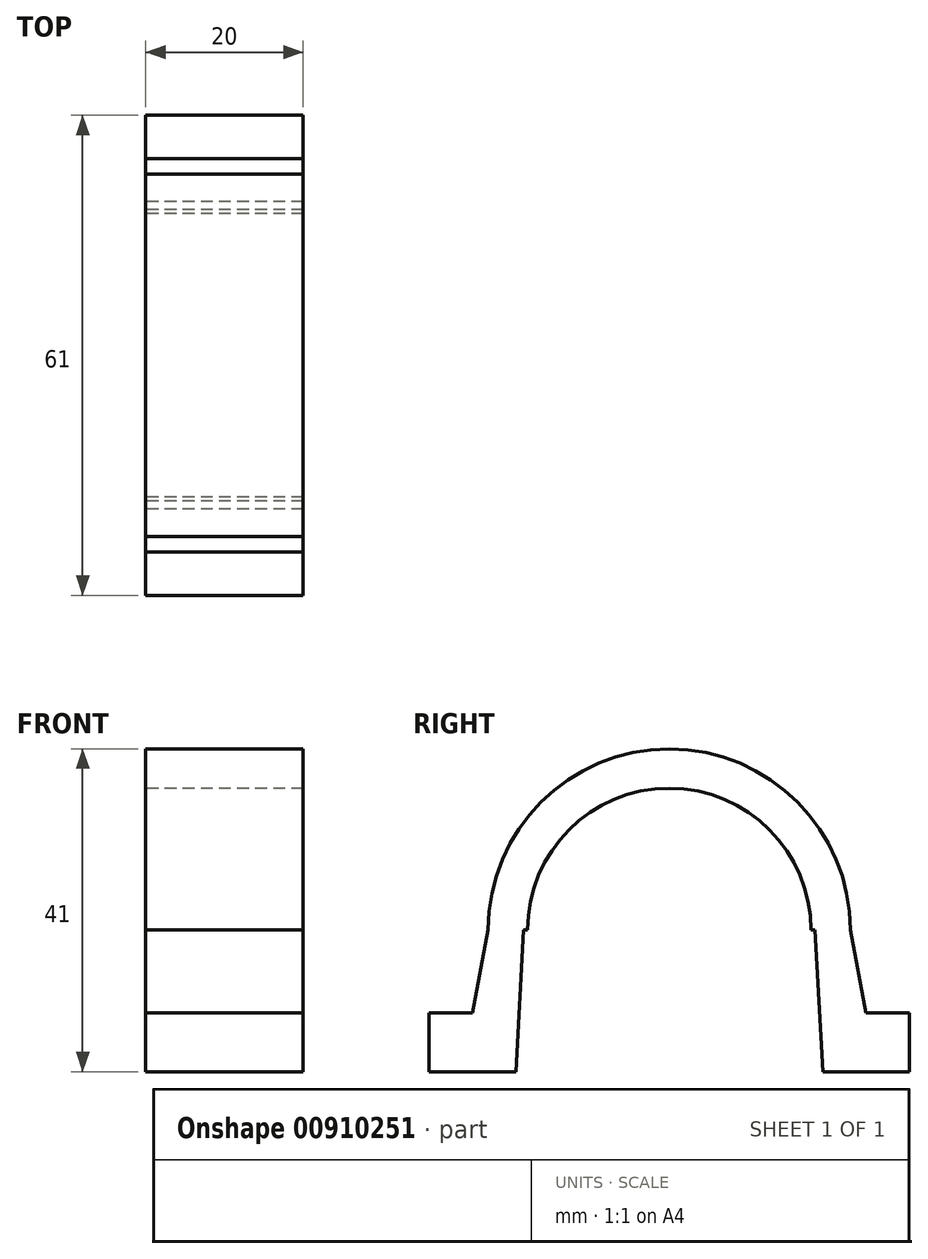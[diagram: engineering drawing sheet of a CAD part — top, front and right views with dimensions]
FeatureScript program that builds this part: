
annotation { "Feature Type Name" : "Feature", "Feature Type Description" : "" }
export const myFeature = defineFeature(function(context is Context, id is Id, definition is map)
    precondition{}
    {
        {
            var Q0;
            Q0=qCreatedBy(makeId("Right.planeOp"),FACE);
            var sketch = newSketch(context, id + "F0", { "sketchPlane" : qUnion([Q0])});
            skCircle(sketch, "E0", {"center": v(0, 0) * mm, "radius": 18 * mm});
            skCircle(sketch, "E1", {"center": v(0, 0) * mm, "radius": 23 * mm});
            skLineSegment(sketch, "E2.bottom", {"start": v(-30.5, -10) * mm, "end": v(30.5, -10) * mm});
            skLineSegment(sketch, "E2.top", {"start": v(-30.5, 10) * mm, "end": v(30.5, 10) * mm});
            skLineSegment(sketch, "E2.left", {"start": v(-30.5, -10) * mm, "end": v(-30.5, 10) * mm});
            skLineSegment(sketch, "E2.right", {"start": v(30.5, -10) * mm, "end": v(30.5, 10) * mm});
            skLineSegment(sketch, "E3", {"start": v(-30.5, 0) * mm, "end": v(30.5, 0) * mm});
            skLineSegment(sketch, "E4", {"start": v(0, 0) * mm, "end": v(0, -18) * mm});
            skPoint(sketch, "E4.endSnap0", {"position": v(0, -10) * mm});
            skLineSegment(sketch, "E5", {"start": v(0, -18) * mm, "end": v(30.5, -18) * mm});
            skLineSegment(sketch, "E6", {"start": v(0, -18) * mm, "end": v(-30.5, -18) * mm});
            skLineSegment(sketch, "E7", {"start": v(18, 0) * mm, "end": v(18.5, 0) * mm});
            skLineSegment(sketch, "E8", {"start": v(18.5, 0) * mm, "end": v(18.5, -18) * mm});
            skLineSegment(sketch, "E9", {"start": v(18.5, -18) * mm, "end": v(19.5, -18) * mm});
            skLineSegment(sketch, "E10", {"start": v(18.5, 0) * mm, "end": v(19.5, -18) * mm});
            skLineSegment(sketch, "E11", {"start": v(30.5, 0) * mm, "end": v(30.5, -18) * mm});
            skLineSegment(sketch, "E12", {"start": v(30.5, -18) * mm, "end": v(30.5, -10.5) * mm});
            skLineSegment(sketch, "E13", {"start": v(30.5, -10.5) * mm, "end": v(18.5, -10.5) * mm});
            skLineSegment(sketch, "E14", {"start": v(23, 0) * mm, "end": v(23, -10.5) * mm});
            skLineSegment(sketch, "E15", {"start": v(23, -10.5) * mm, "end": v(25, -10.5) * mm});
            skLineSegment(sketch, "E16", {"start": v(23, 0) * mm, "end": v(25, -10.5) * mm});
            skPoint(sketch, "E17.end.orphan", {"position": v(25, -18) * mm});
            skLineSegment(sketch, "E18.MirrorCS", {"start": v(-23, 0) * mm, "end": v(-25, -10.5) * mm});
            skLineSegment(sketch, "E19.MirrorCS", {"start": v(-30.5, -10.5) * mm, "end": v(-18.5, -10.5) * mm});
            skLineSegment(sketch, "E20.MirrorCS", {"start": v(-30.5, 0) * mm, "end": v(-30.5, -18) * mm});
            skLineSegment(sketch, "E21.MirrorCS", {"start": v(-18.5, 0) * mm, "end": v(-19.5, -18) * mm});
            skLineSegment(sketch, "E22.MirrorCS", {"start": v(-18, 0) * mm, "end": v(-18.5, 0) * mm});
            skSolve(sketch);
        }
        {
            var Q0;
            {var subQ4=sQuery(id+"F0.wireOp",EDGE,"E2.top");var subQ5=sQuery(id+"F0.wireOp",EDGE,"E0");var subQ6=makeQuery(id+"F0.imprint","INTERSECT",VERTEX,{"disambiguationData":[OD(0.0)],"derivedFrom":[subQ5,subQ4]});Q0=makeQuery(id+"F0.imprint","IMPRINT",FACE,{"disambiguationData":[TD([[makeQuery(id+"F0.imprint","IMPRINT",EDGE,{"disambiguationData":[TD([[subQ6,-1.0]])],"derivedFrom":subQ5}),-1.0]])]});}
            var Q1;
            {var subQ0=sQuery(id+"F0.wireOp",EDGE,"E2.top");var subQ1=sQuery(id+"F0.wireOp",EDGE,"E0");var subQ2=makeQuery(id+"F0.imprint","INTERSECT",VERTEX,{"disambiguationData":[OD(0.0)],"derivedFrom":[subQ1,subQ0]});Q1=makeQuery(id+"F0.imprint","IMPRINT",FACE,{"disambiguationData":[TD([[makeQuery(id+"F0.imprint","IMPRINT",EDGE,{"disambiguationData":[TD([[subQ2,1.0]])],"derivedFrom":subQ1}),-1.0]])]});}
            var Q2;
            {var subQ0=sQuery(id+"F0.wireOp",EDGE,"E3");var subQ6=sQuery(id+"F0.wireOp",EDGE,"E0");var subQ8=makeQuery(id+"F0.imprint","INTERSECT",VERTEX,{"disambiguationData":[OD(1.0)],"derivedFrom":[subQ6,subQ0]});Q2=makeQuery(id+"F0.imprint","IMPRINT",FACE,{"disambiguationData":[TD([[makeQuery(id+"F0.imprint","IMPRINT",EDGE,{"disambiguationData":[TD([[subQ8,-1.0]])],"derivedFrom":subQ6}),-1.0]])]});}
            var Q3;
            {var subQ1=sQuery(id+"F0.wireOp",EDGE,"E1");var subQ3=sQuery(id+"F0.wireOp",EDGE,"E2.bottom");var subQ4=makeQuery(id+"F0.imprint","INTERSECT",VERTEX,{"disambiguationData":[OD(1.0)],"derivedFrom":[subQ1,subQ3]});Q3=makeQuery(id+"F0.imprint","IMPRINT",FACE,{"disambiguationData":[TD([[makeQuery(id+"F0.imprint","IMPRINT",EDGE,{"disambiguationData":[TD([[subQ4,-1.0]])],"derivedFrom":subQ3}),1.0]])]});}
            var Q4;
            {var subQ1=sQuery(id+"F0.wireOp",EDGE,"E1");var subQ3=sQuery(id+"F0.wireOp",EDGE,"E2.bottom");var subQ4=makeQuery(id+"F0.imprint","INTERSECT",VERTEX,{"disambiguationData":[OD(1.0)],"derivedFrom":[subQ1,subQ3]});Q4=makeQuery(id+"F0.imprint","IMPRINT",FACE,{"disambiguationData":[TD([[makeQuery(id+"F0.imprint","IMPRINT",EDGE,{"disambiguationData":[TD([[subQ4,1.0]])],"derivedFrom":subQ3}),1.0]])]});}
            var Q5;
            {var subQ0=sQuery(id+"F0.wireOp",EDGE,"E2.bottom");var subQ1=sQuery(id+"F0.wireOp",EDGE,"E1");var subQ2=makeQuery(id+"F0.imprint","INTERSECT",VERTEX,{"disambiguationData":[OD(1.0)],"derivedFrom":[subQ1,subQ0]});Q5=makeQuery(id+"F0.imprint","IMPRINT",FACE,{"disambiguationData":[TD([[makeQuery(id+"F0.imprint","IMPRINT",EDGE,{"disambiguationData":[TD([[subQ2,-1.0]])],"derivedFrom":subQ1}),1.0]])]});}
            var Q6;
            {var subQ0=sQuery(id+"F0.wireOp",EDGE,"E2.bottom");var subQ1=sQuery(id+"F0.wireOp",EDGE,"E1");var subQ2=makeQuery(id+"F0.imprint","INTERSECT",VERTEX,{"disambiguationData":[OD(1.0)],"derivedFrom":[subQ1,subQ0]});Q6=makeQuery(id+"F0.imprint","IMPRINT",FACE,{"disambiguationData":[TD([[makeQuery(id+"F0.imprint","IMPRINT",EDGE,{"disambiguationData":[TD([[subQ2,-1.0]])],"derivedFrom":subQ1}),-1.0]])]});}
            var Q7;
            {var subQ0=sQuery(id+"F0.wireOp",EDGE,"E19.MirrorCS");var subQ1=sQuery(id+"F0.wireOp",EDGE,"E1");var subQ2=makeQuery(id+"F0.imprint","INTERSECT",VERTEX,{"derivedFrom":[subQ1,subQ0]});Q7=makeQuery(id+"F0.imprint","IMPRINT",FACE,{"disambiguationData":[TD([[makeQuery(id+"F0.imprint","IMPRINT",EDGE,{"disambiguationData":[TD([[subQ2,-1.0]])],"derivedFrom":subQ1}),1.0]])]});}
            var Q8;
            {var subQ0=sQuery(id+"F0.wireOp",EDGE,"E19.MirrorCS");var subQ2=sQuery(id+"F0.wireOp",EDGE,"E1");var subQ3=makeQuery(id+"F0.imprint","INTERSECT",VERTEX,{"derivedFrom":[subQ2,subQ0]});Q8=makeQuery(id+"F0.imprint","IMPRINT",FACE,{"disambiguationData":[TD([[makeQuery(id+"F0.imprint","IMPRINT",EDGE,{"disambiguationData":[TD([[subQ3,-1.0]])],"derivedFrom":subQ2}),-1.0]])]});}
            var Q9;
            {var subQ0=sQuery(id+"F0.wireOp",EDGE,"E16");var subQ1=sQuery(id+"F0.wireOp",EDGE,"E2.bottom");var subQ2=makeQuery(id+"F0.imprint","INTERSECT",VERTEX,{"derivedFrom":[subQ1,subQ0]});Q9=makeQuery(id+"F0.imprint","IMPRINT",FACE,{"disambiguationData":[TD([[makeQuery(id+"F0.imprint","IMPRINT",EDGE,{"disambiguationData":[TD([[subQ2,1.0]])],"derivedFrom":subQ1}),1.0]])]});}
            var Q10;
            {var subQ3=sQuery(id+"F0.wireOp",EDGE,"E2.bottom");var subQ5=sQuery(id+"F0.wireOp",EDGE,"E10");var subQ6=makeQuery(id+"F0.imprint","INTERSECT",VERTEX,{"derivedFrom":[subQ3,subQ5]});Q10=makeQuery(id+"F0.imprint","IMPRINT",FACE,{"disambiguationData":[TD([[makeQuery(id+"F0.imprint","IMPRINT",EDGE,{"disambiguationData":[TD([[subQ6,-1.0]])],"derivedFrom":subQ3}),1.0]])]});}
            var Q11;
            {var subQ1=sQuery(id+"F0.wireOp",EDGE,"E1");var subQ3=sQuery(id+"F0.wireOp",EDGE,"E2.bottom");var subQ4=makeQuery(id+"F0.imprint","INTERSECT",VERTEX,{"disambiguationData":[OD(0.0)],"derivedFrom":[subQ1,subQ3]});Q11=makeQuery(id+"F0.imprint","IMPRINT",FACE,{"disambiguationData":[TD([[makeQuery(id+"F0.imprint","IMPRINT",EDGE,{"disambiguationData":[TD([[subQ4,-1.0]])],"derivedFrom":subQ3}),1.0]])]});}
            var Q12;
            {var subQ5=sQuery(id+"F0.wireOp",EDGE,"E10");var subQ7=sQuery(id+"F0.wireOp",EDGE,"E1");var subQ8=makeQuery(id+"F0.imprint","INTERSECT",VERTEX,{"derivedFrom":[subQ7,subQ5]});Q12=makeQuery(id+"F0.imprint","IMPRINT",FACE,{"disambiguationData":[TD([[makeQuery(id+"F0.imprint","IMPRINT",EDGE,{"disambiguationData":[TD([[subQ8,-1.0]])],"derivedFrom":subQ7}),-1.0]])]});}
            var Q13;
            {var subQ0=sQuery(id+"F0.wireOp",EDGE,"E10");var subQ1=sQuery(id+"F0.wireOp",EDGE,"E1");var subQ2=makeQuery(id+"F0.imprint","INTERSECT",VERTEX,{"derivedFrom":[subQ1,subQ0]});Q13=makeQuery(id+"F0.imprint","IMPRINT",FACE,{"disambiguationData":[TD([[makeQuery(id+"F0.imprint","IMPRINT",EDGE,{"disambiguationData":[TD([[subQ2,-1.0]])],"derivedFrom":subQ1}),1.0]])]});}
            var Q14;
            {var subQ0=sQuery(id+"F0.wireOp",EDGE,"E13");var subQ1=sQuery(id+"F0.wireOp",EDGE,"E1");var subQ2=makeQuery(id+"F0.imprint","INTERSECT",VERTEX,{"derivedFrom":[subQ1,subQ0]});Q14=makeQuery(id+"F0.imprint","IMPRINT",FACE,{"disambiguationData":[TD([[makeQuery(id+"F0.imprint","IMPRINT",EDGE,{"disambiguationData":[TD([[subQ2,-1.0]])],"derivedFrom":subQ1}),1.0]])]});}
            var Q15;
            {var subQ0=sQuery(id+"F0.wireOp",EDGE,"E13");var subQ1=sQuery(id+"F0.wireOp",EDGE,"E1");var subQ2=makeQuery(id+"F0.imprint","INTERSECT",VERTEX,{"derivedFrom":[subQ1,subQ0]});Q15=makeQuery(id+"F0.imprint","IMPRINT",FACE,{"disambiguationData":[TD([[makeQuery(id+"F0.imprint","IMPRINT",EDGE,{"disambiguationData":[TD([[subQ2,-1.0]])],"derivedFrom":subQ1}),-1.0]])]});}
            var Q16;
            {var subQ0=sQuery(id+"F0.wireOp",EDGE,"E16");var subQ1=sQuery(id+"F0.wireOp",EDGE,"E2.bottom");var subQ2=makeQuery(id+"F0.imprint","INTERSECT",VERTEX,{"derivedFrom":[subQ1,subQ0]});Q16=makeQuery(id+"F0.imprint","IMPRINT",FACE,{"disambiguationData":[TD([[makeQuery(id+"F0.imprint","IMPRINT",EDGE,{"disambiguationData":[TD([[subQ2,1.0]])],"derivedFrom":subQ1}),-1.0]])]});}
            extrude(context, id + "F1", {"entities" : qUnion([Q0, Q1, Q2, Q3, Q4, Q5, Q6, Q7, Q8, Q9, Q10, Q11, Q12, Q13, Q14, Q15, Q16]), "depth" : 20 * mm, "offsetDistance" : 25 * mm});
        }
    });
